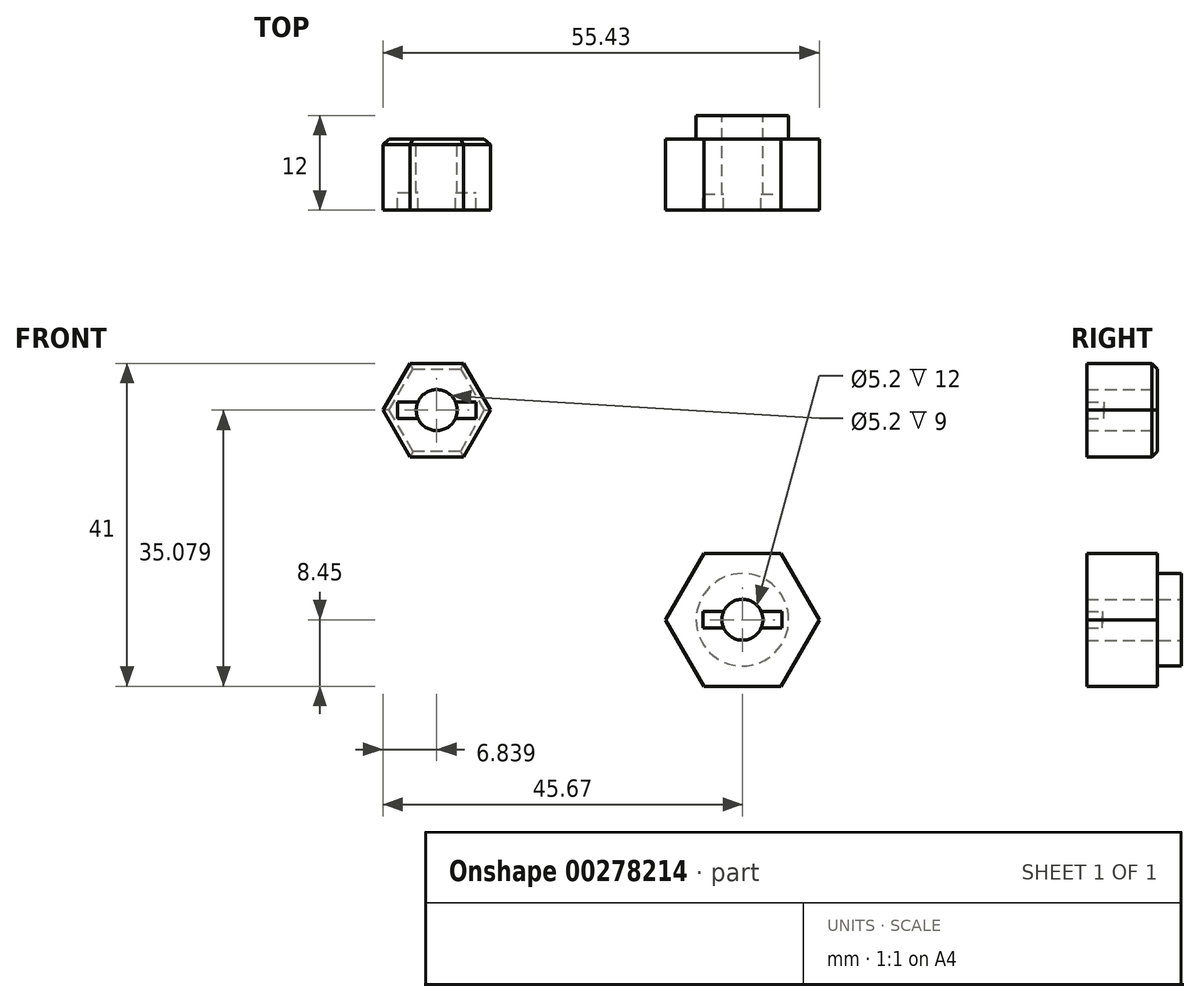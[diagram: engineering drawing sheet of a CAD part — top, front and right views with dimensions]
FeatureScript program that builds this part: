
annotation { "Feature Type Name" : "Feature", "Feature Type Description" : "" }
export const myFeature = defineFeature(function(context is Context, id is Id, definition is map)
    precondition{}
    {
        {
            var Q0;
            Q0=qCreatedBy(makeId("Front.planeOp"),FACE);
            var sketch = newSketch(context, id + "F0", { "sketchPlane" : qUnion([Q0])});
            skCircle(sketch, "E0.cCircle", {"center": v(-38.83, 26.13) * mm, "radius": 5.92 * mm, "construction": true});
            skLineSegment(sketch, "E0.0", {"start": v(-42.25, 32.05) * mm, "end": v(-35.4, 32.05) * mm});
            skLineSegment(sketch, "E0.1", {"start": v(-35.4, 32.05) * mm, "end": v(-31.99, 26.13) * mm});
            skLineSegment(sketch, "E0.2", {"start": v(-31.99, 26.13) * mm, "end": v(-35.4, 20.2) * mm});
            skLineSegment(sketch, "E0.3", {"start": v(-35.4, 20.2) * mm, "end": v(-42.25, 20.2) * mm});
            skLineSegment(sketch, "E0.4", {"start": v(-42.25, 20.2) * mm, "end": v(-45.67, 26.13) * mm});
            skLineSegment(sketch, "E0.5", {"start": v(-45.67, 26.13) * mm, "end": v(-42.25, 32.05) * mm});
            skPoint(sketch, "E0.0.midPoint", {"position": v(-38.83, 32.05) * mm});
            skCircle(sketch, "E1", {"center": v(-38.83, 26.13) * mm, "radius": 2.6 * mm});
            skLineSegment(sketch, "E2", {"start": v(-38.83, 26.13) * mm, "end": v(-38.83, 27.18) * mm});
            skLineSegment(sketch, "E3", {"start": v(-38.83, 27.18) * mm, "end": v(-43.83, 27.18) * mm});
            skLineSegment(sketch, "E4", {"start": v(-43.83, 27.18) * mm, "end": v(-43.83, 25.08) * mm});
            skLineSegment(sketch, "E5", {"start": v(-43.83, 25.08) * mm, "end": v(-33.83, 25.08) * mm});
            skLineSegment(sketch, "E6", {"start": v(-33.83, 25.08) * mm, "end": v(-33.83, 27.18) * mm});
            skLineSegment(sketch, "E7", {"start": v(-33.83, 27.18) * mm, "end": v(-38.83, 27.18) * mm});
            skSolve(sketch);
        }
        {
            var Q0;
            Q0=makeQuery(id+"F0.imprint","IMPRINT",FACE,{"disambiguationData":[TD([[makeQuery(id+"F0.imprint","IMPRINT",EDGE,{"derivedFrom":sQuery(id+"F0.wireOp",EDGE,"E0.0")}),-1.0]])]});
            extrude(context, id + "F1", {"entities" : qUnion([Q0]), "depth" : 9 * mm});
        }
        {
            var Q0;
            {var subQ5=sQuery(id+"F0.wireOp",EDGE,"E4");Q0=makeQuery(id+"F0.imprint","IMPRINT",FACE,{"disambiguationData":[TD([[makeQuery(id+"F0.imprint","IMPRINT",EDGE,{"derivedFrom":subQ5}),1.0]])]});}
            var Q1;
            {var subQ5=sQuery(id+"F0.wireOp",EDGE,"E6");Q1=makeQuery(id+"F0.imprint","IMPRINT",FACE,{"disambiguationData":[TD([[makeQuery(id+"F0.imprint","IMPRINT",EDGE,{"derivedFrom":subQ5}),1.0]])]});}
            extrude(context, id + "F2", {"entities" : qUnion([Q0, Q1]), "operationType" : NewBodyOperationType.ADD, "depth" : 6.8 * mm});
        }
        {
            var Q0;
            Q0=makeQuery(id+"F1.opExtrude","CAP_EDGE",EDGE,{"disambiguationData":[OSD([sQuery(id+"F0.wireOp",EDGE,"E0.1")])],"isStart":true});
            var Q1;
            Q1=makeQuery(id+"F1.opExtrude","CAP_EDGE",EDGE,{"disambiguationData":[OSD([sQuery(id+"F0.wireOp",EDGE,"E0.2")])],"isStart":true});
            var Q2;
            Q2=makeQuery(id+"F1.opExtrude","CAP_EDGE",EDGE,{"disambiguationData":[OSD([sQuery(id+"F0.wireOp",EDGE,"E0.3")])],"isStart":true});
            var Q3;
            Q3=makeQuery(id+"F1.opExtrude","CAP_EDGE",EDGE,{"disambiguationData":[OSD([sQuery(id+"F0.wireOp",EDGE,"E0.4")])],"isStart":true});
            var Q4;
            Q4=makeQuery(id+"F1.opExtrude","CAP_EDGE",EDGE,{"disambiguationData":[OSD([sQuery(id+"F0.wireOp",EDGE,"E0.5")])],"isStart":true});
            var Q5;
            Q5=makeQuery(id+"F1.opExtrude","CAP_EDGE",EDGE,{"disambiguationData":[OSD([sQuery(id+"F0.wireOp",EDGE,"E0.0")])],"isStart":true});
            chamfer(context, id + "F3", {"entities" : qUnion([Q0, Q1, Q2, Q3, Q4, Q5]), "width" : .7 * mm, "tangentPropagation" : true});
        }
        {
            var Q0;
            Q0=qCreatedBy(makeId("Front.planeOp"),FACE);
            var sketch = newSketch(context, id + "F4", { "sketchPlane" : qUnion([Q0])});
            skCircle(sketch, "E8.cCircle", {"center": v(0, -0.5) * mm, "radius": 8.45 * mm, "construction": true});
            skLineSegment(sketch, "E8.0", {"start": v(-4.88, 7.95) * mm, "end": v(4.88, 7.95) * mm});
            skLineSegment(sketch, "E8.1", {"start": v(4.88, 7.95) * mm, "end": v(9.76, -0.5) * mm});
            skLineSegment(sketch, "E8.2", {"start": v(9.76, -0.5) * mm, "end": v(4.88, -8.95) * mm});
            skLineSegment(sketch, "E8.3", {"start": v(4.88, -8.95) * mm, "end": v(-4.88, -8.95) * mm});
            skLineSegment(sketch, "E8.4", {"start": v(-4.88, -8.95) * mm, "end": v(-9.76, -0.5) * mm});
            skLineSegment(sketch, "E8.5", {"start": v(-9.76, -0.5) * mm, "end": v(-4.88, 7.95) * mm});
            skPoint(sketch, "E8.0.midPoint", {"position": v(0, 7.95) * mm});
            skCircle(sketch, "E9", {"center": v(0, -0.5) * mm, "radius": 2.6 * mm});
            skLineSegment(sketch, "E10", {"start": v(0, -0.5) * mm, "end": v(0, 0.55) * mm});
            skLineSegment(sketch, "E11", {"start": v(0, 0.55) * mm, "end": v(-5, 0.55) * mm});
            skLineSegment(sketch, "E12", {"start": v(-5, 0.55) * mm, "end": v(-5, -1.55) * mm});
            skLineSegment(sketch, "E13", {"start": v(-5, -1.55) * mm, "end": v(5, -1.55) * mm});
            skLineSegment(sketch, "E14", {"start": v(5, -1.55) * mm, "end": v(5, 0.55) * mm});
            skLineSegment(sketch, "E15", {"start": v(5, 0.55) * mm, "end": v(0, 0.55) * mm});
            skCircle(sketch, "E16", {"center": v(0, -0.5) * mm, "radius": 5.88 * mm});
            skSolve(sketch);
        }
        {
            var Q0;
            Q0=makeQuery(id+"F4.imprint","IMPRINT",FACE,{"disambiguationData":[TD([[makeQuery(id+"F4.imprint","IMPRINT",EDGE,{"derivedFrom":sQuery(id+"F4.wireOp",EDGE,"E8.0")}),-1.0]])]});
            var Q1;
            {var subQ0=sQuery(id+"F4.wireOp",EDGE,"E12");Q1=makeQuery(id+"F4.imprint","IMPRINT",FACE,{"disambiguationData":[TD([[makeQuery(id+"F4.imprint","IMPRINT",EDGE,{"derivedFrom":subQ0}),-1.0]])]});}
            extrude(context, id + "F5", {"entities" : qUnion([Q0, Q1]), "depth" : 9 * mm});
        }
        {
            var Q0;
            {var subQ5=sQuery(id+"F4.wireOp",EDGE,"E12");Q0=makeQuery(id+"F4.imprint","IMPRINT",FACE,{"disambiguationData":[TD([[makeQuery(id+"F4.imprint","IMPRINT",EDGE,{"derivedFrom":subQ5}),1.0]])]});}
            var Q1;
            {var subQ5=sQuery(id+"F4.wireOp",EDGE,"E14");Q1=makeQuery(id+"F4.imprint","IMPRINT",FACE,{"disambiguationData":[TD([[makeQuery(id+"F4.imprint","IMPRINT",EDGE,{"derivedFrom":subQ5}),1.0]])]});}
            extrude(context, id + "F6", {"entities" : qUnion([Q0, Q1]), "operationType" : NewBodyOperationType.ADD, "depth" : 7 * mm});
        }
        {
            var Q0;
            {var subQ0=sQuery(id+"F4.wireOp",EDGE,"E12");Q0=makeQuery(id+"F4.imprint","IMPRINT",FACE,{"disambiguationData":[TD([[makeQuery(id+"F4.imprint","IMPRINT",EDGE,{"derivedFrom":subQ0}),-1.0]])]});}
            var Q1;
            {var subQ5=sQuery(id+"F4.wireOp",EDGE,"E12");Q1=makeQuery(id+"F4.imprint","IMPRINT",FACE,{"disambiguationData":[TD([[makeQuery(id+"F4.imprint","IMPRINT",EDGE,{"derivedFrom":subQ5}),1.0]])]});}
            var Q2;
            {var subQ5=sQuery(id+"F4.wireOp",EDGE,"E14");Q2=makeQuery(id+"F4.imprint","IMPRINT",FACE,{"disambiguationData":[TD([[makeQuery(id+"F4.imprint","IMPRINT",EDGE,{"derivedFrom":subQ5}),1.0]])]});}
            extrude(context, id + "F7", {"entities" : qUnion([Q0, Q1, Q2]), "operationType" : NewBodyOperationType.ADD, "oppositeDirection" : true, "depth" : 3 * mm});
        }
    });
